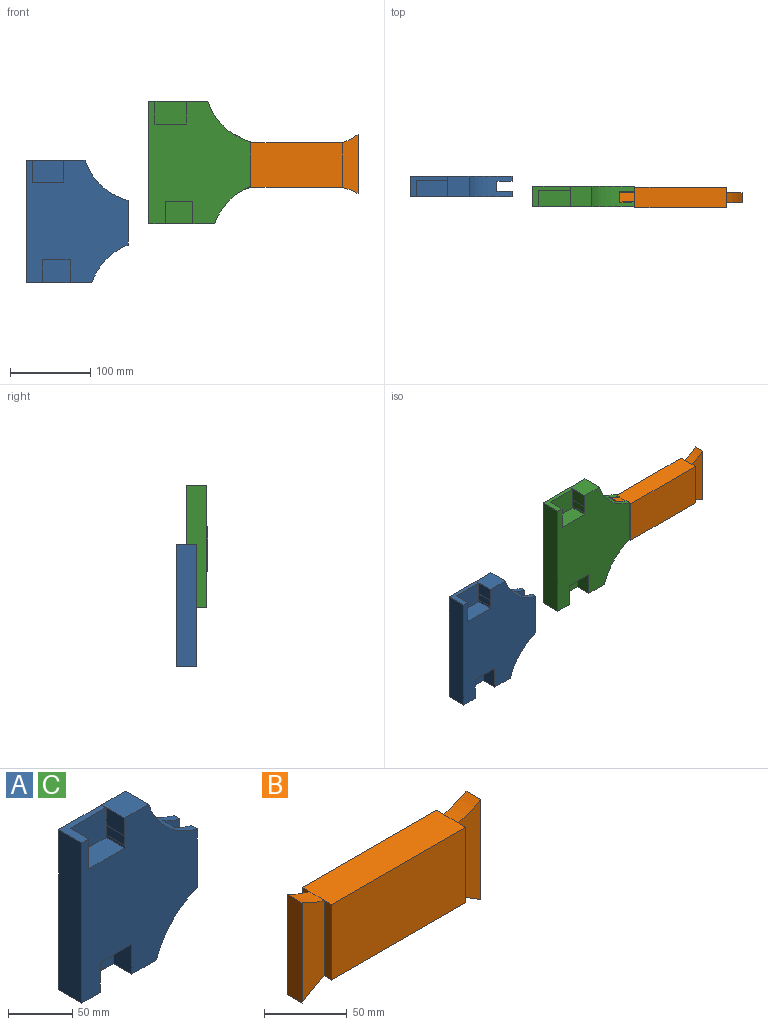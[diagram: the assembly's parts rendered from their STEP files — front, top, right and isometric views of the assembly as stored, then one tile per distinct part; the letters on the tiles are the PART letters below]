
ASSEMBLY  parts=3 mates=1
PART A: 28 faces, bbox 127x25.4x152.4 mm
  f0: plane 55.57x6.35mm, normal (1,0,0), area 352.9mm2, adj f2,f19,f21,f26
  f1: plane 55.57x6.35mm, normal (1,0,0), area 352.9mm2, adj f2,f19,f20,f27
  f2: cylinder r=76.2mm len=53.55mm, axis (0,1,0), area 1683.1mm2, adj f0,f1,f3,f20,f21,f25,f26,f27
  f3: plane 26.37x25.4mm, normal (0,0,1), area 669.8mm2, adj f2,f4,f20,f21
  f4: cylinder r=101.6mm len=25.4mm, axis (0,1,0), area 0.2mm2, adj f3,f5,f20,f21
  f5: plane 25.4x0.33mm, normal (0.02,0,1), area 1.7mm2, adj f4,f6,f12,f20,f21,f23
  f6: plane 20.32x16.8mm, normal (-1,0,0), area 341.4mm2, adj f5,f7,f20,f23
  f7: plane 25.4x0.08mm, normal (0,0,-1), area 2.1mm2, adj f6,f8,f20,f21,f22
  f8: plane 25.4x9.27mm, normal (-1,0,0.01), area 235.5mm2, adj f7,f9,f20,f21,f22
  f9: plane 20.32x2.41mm, normal (-1,0,0), area 48.9mm2, adj f8,f10,f20,f23
  f10: plane 39.45x20.32mm, normal (0,0,1), area 801.5mm2, adj f9,f11,f20,f23
  f11: plane 28.49x20.32mm, normal (1,0,0), area 578.8mm2, adj f10,f12,f20,f23
  f12: plane 46.75x25.4mm, normal (0,0,1), area 392.5mm2, adj f5,f11,f13,f20,f21,f23
  f13: plane 25.4x0.17mm, normal (-1,0,0.02), area 4.3mm2, adj f12,f14,f20,f21
  f14: plane 152.23x25.4mm, normal (-1,0,0), area 3866.7mm2, adj f13,f15,f20,f21
  f15: plane 82.01x25.4mm, normal (0,0,-1), area 1384.5mm2, adj f14,f16,f18,f19,f20,f21,f24
  f16: plane 28.37x20.32mm, normal (1,0,0), area 576.5mm2, adj f15,f17,f20,f24
  f17: plane 34.37x20.32mm, normal (0,0,-1), area 698.4mm2, adj f16,f18,f20,f24
  f18: plane 28.37x20.32mm, normal (-1,0,0), area 576.5mm2, adj f15,f17,f20,f24
  f19: cylinder r=76.2mm len=46.64mm, axis (0,1,0), area 1422.4mm2, adj f0,f1,f15,f20,f21,f25,f26,f27
  f20: plane 152.4x127mm, normal (0,-1,0), area 14080.1mm2, adj f1,f2,f3,f4,f5,f6,f7,f8
  f21: plane 152.4x127mm, normal (0,1,0), area 16178.9mm2, adj f0,f2,f3,f4,f5,f7,f8,f12
  f22: plane 9.27x5.08mm, normal (1,0,0), area 47.1mm2, adj f7,f8,f21,f23
  f23: plane 39.45x28.49mm, normal (0,-1,0), area 1123.6mm2, adj f5,f6,f9,f10,f11,f12,f22
  f24: plane 34.37x28.37mm, normal (0,-1,0), area 975.2mm2, adj f15,f16,f17,f18
  f25: plane 73.91x12.7mm, normal (1,0,0), area 938.6mm2, adj f2,f19,f26,f27
  f26: plane 73.91x19.05mm, normal (0,-1,0), area 1212.3mm2, adj f0,f2,f19,f25
  f27: plane 73.91x19.05mm, normal (0,1,0), area 1212.3mm2, adj f1,f2,f19,f25
PART B: 18 faces, bbox 152.4x25.4x73.9 mm
  f0: plane 73.91x12.7mm, normal (1,0,0), area 938.6mm2, adj f3,f4,f13,f17
  f1: plane 73.91x12.7mm, normal (-1,0,0), area 938.6mm2, adj f2,f5,f11,f15
  f2: cylinder r=76.2mm len=19.05mm, axis (0,-1,0), area 277.8mm2, adj f1,f6,f11,f15
  f3: cylinder r=76.2mm len=19.05mm, axis (0,-1,0), area 277.8mm2, adj f0,f6,f13,f17
  f4: cylinder r=76.2mm len=19.05mm, axis (0,-1,0), area 261.9mm2, adj f0,f7,f13,f17
  f5: cylinder r=76.2mm len=19.05mm, axis (0,-1,0), area 261.9mm2, adj f1,f7,f11,f15
  f6: plane 114.3x25.4mm, normal (0,0,-1), area 2903.2mm2, adj f2,f3,f8,f9,f10,f12,f14,f16
  f7: plane 114.3x25.4mm, normal (0,0,1), area 2903.2mm2, adj f4,f5,f8,f9,f10,f12,f14,f16
  f8: plane 114.3x55.57mm, normal (0,1,0), area 6351.6mm2, adj f6,f7,f14,f16
  f9: plane 114.3x55.57mm, normal (0,-1,0), area 6351.6mm2, adj f6,f7,f10,f12
  f10: plane 55.57x6.35mm, normal (-1,0,0), area 352.9mm2, adj f6,f7,f9,f11
  f11: plane 73.91x19.05mm, normal (0,-1,0), area 1212.3mm2, adj f1,f2,f5,f10
  f12: plane 55.57x6.35mm, normal (1,0,0), area 352.9mm2, adj f6,f7,f9,f13
  f13: plane 73.91x19.05mm, normal (0,-1,0), area 1212.3mm2, adj f0,f3,f4,f12
  f14: plane 55.57x6.35mm, normal (-1,0,0), area 352.9mm2, adj f6,f7,f8,f15
  f15: plane 73.91x19.05mm, normal (0,1,0), area 1212.3mm2, adj f1,f2,f5,f14
  f16: plane 55.57x6.35mm, normal (1,0,0), area 352.9mm2, adj f6,f7,f8,f17
  f17: plane 73.91x19.05mm, normal (0,1,0), area 1212.3mm2, adj f0,f3,f4,f16
PART C: same geometry as A
PLACE A t=(-5.82,25.4,58.13)mm
PLACE B rot(axis=(0,1,0),180deg) t=(404.83,-14.15,72.64)mm
PLACE C t=(147.1,12.71,131.05)mm
MATE planar B.f0 <-> C.f25  axis (-1,0,0) through (202.67,-1.45,73.57)mm
